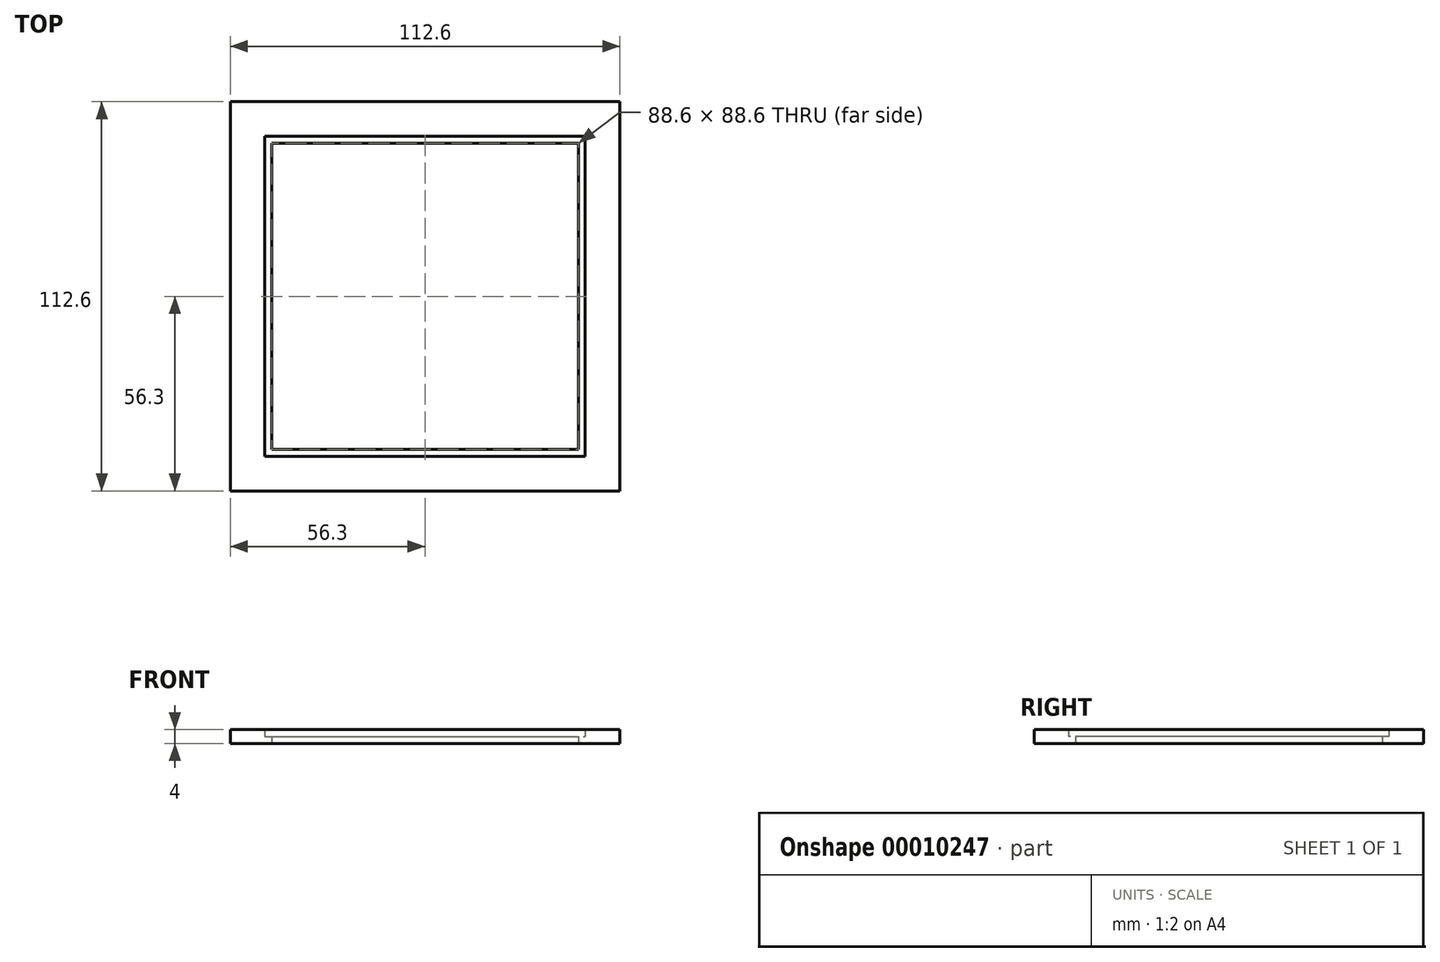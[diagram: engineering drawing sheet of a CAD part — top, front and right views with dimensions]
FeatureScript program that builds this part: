
annotation { "Feature Type Name" : "Feature", "Feature Type Description" : "" }
export const myFeature = defineFeature(function(context is Context, id is Id, definition is map)
    precondition{}
    {
        {
            var Q0;
            Q0=qCreatedBy(makeId("Top.planeOp"),FACE);
            var sketch = newSketch(context, id + "F0", { "sketchPlane" : qUnion([Q0])});
            skLineSegment(sketch, "E0.bottom", {"start": v(-46.3, 46.3) * mm, "end": v(46.3, 46.3) * mm});
            skLineSegment(sketch, "E0.top", {"start": v(-46.3, -46.3) * mm, "end": v(46.3, -46.3) * mm});
            skLineSegment(sketch, "E0.left", {"start": v(-46.3, 46.3) * mm, "end": v(-46.3, -46.3) * mm});
            skLineSegment(sketch, "E0.right", {"start": v(46.3, 46.3) * mm, "end": v(46.3, -46.3) * mm});
            skLineSegment(sketch, "E1.0", {"start": v(-56.3, 56.3) * mm, "end": v(56.3, 56.3) * mm});
            skLineSegment(sketch, "E1.1", {"start": v(-56.3, 56.3) * mm, "end": v(-56.3, -56.3) * mm});
            skLineSegment(sketch, "E1.2", {"start": v(-56.3, -56.3) * mm, "end": v(56.3, -56.3) * mm});
            skLineSegment(sketch, "E1.3", {"start": v(56.3, 56.3) * mm, "end": v(56.3, -56.3) * mm});
            skPoint(sketch, "E2", {"position": v(-46.3, 0) * mm});
            skPoint(sketch, "E3", {"position": v(0, 46.3) * mm});
            skSolve(sketch);
        }
        {
            var Q0;
            Q0 = qSketchRegion(id + "F0", true);
            extrude(context, id + "F1", {"entities" : qUnion([Q0]), "depth" : 4 * mm});
        }
        {
            var Q0;
            Q0=qCreatedBy(makeId("Top.planeOp"),FACE);
            var sketch = newSketch(context, id + "F2", { "sketchPlane" : qUnion([Q0])});
            skLineSegment(sketch, "E4.bottom", {"start": v(-46.3, 46.3) * mm, "end": v(46.3, 46.3) * mm});
            skLineSegment(sketch, "E4.top", {"start": v(-46.3, -46.3) * mm, "end": v(46.3, -46.3) * mm});
            skLineSegment(sketch, "E4.left", {"start": v(-46.3, 46.3) * mm, "end": v(-46.3, -46.3) * mm});
            skLineSegment(sketch, "E4.right", {"start": v(46.3, 46.3) * mm, "end": v(46.3, -46.3) * mm});
            skLineSegment(sketch, "E5.0", {"start": v(-44.3, 44.3) * mm, "end": v(44.3, 44.3) * mm});
            skLineSegment(sketch, "E5.1", {"start": v(-44.3, 44.3) * mm, "end": v(-44.3, -44.3) * mm});
            skLineSegment(sketch, "E5.2", {"start": v(-44.3, -44.3) * mm, "end": v(44.3, -44.3) * mm});
            skLineSegment(sketch, "E5.3", {"start": v(44.3, 44.3) * mm, "end": v(44.3, -44.3) * mm});
            skSolve(sketch);
        }
        {
            var Q0;
            Q0 = qSketchRegion(id + "F2", true);
            extrude(context, id + "F3", {"entities" : qUnion([Q0]), "operationType" : NewBodyOperationType.ADD, "depth" : 2 * mm});
        }
    });
